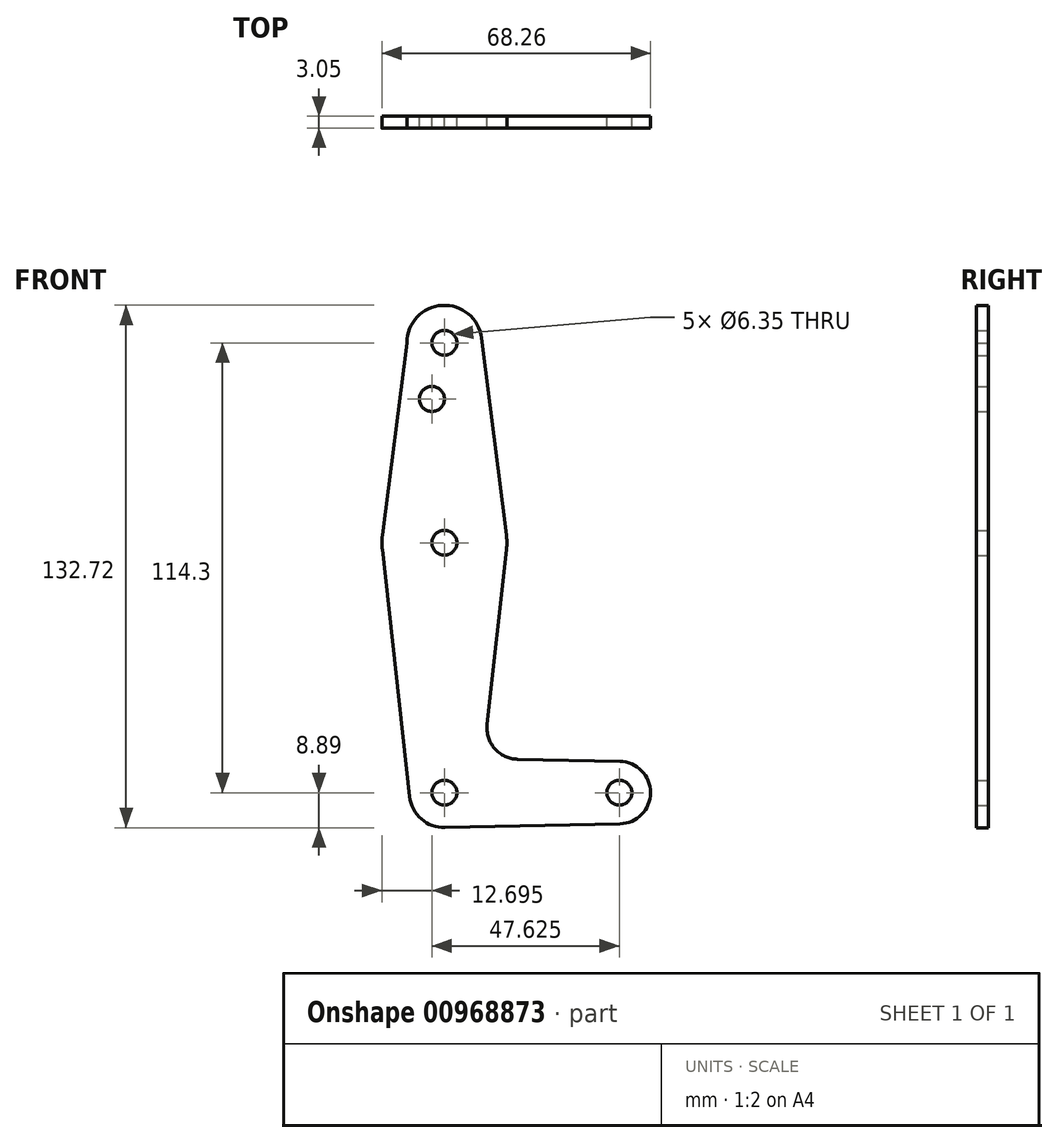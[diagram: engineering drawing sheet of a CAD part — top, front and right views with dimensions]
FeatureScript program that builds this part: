
annotation { "Feature Type Name" : "Feature", "Feature Type Description" : "" }
export const myFeature = defineFeature(function(context is Context, id is Id, definition is map)
    precondition{}
    {
        {
            var Q0;
            Q0=qCreatedBy(makeId("Front.planeOp"),FACE);
            var sketch = newSketch(context, id + "F0", { "sketchPlane" : qUnion([Q0])});
            skCircle(sketch, "E0", {"center": v(0, 114.3) * mm, "radius": 9.53 * mm});
            skCircle(sketch, "E1", {"center": v(0, 63.5) * mm, "radius": 15.88 * mm});
            skCircle(sketch, "E2", {"center": v(0, 0) * mm, "radius": 8.9 * mm});
            skCircle(sketch, "E3", {"center": v(44.45, 0) * mm, "radius": 7.94 * mm});
            skLineSegment(sketch, "E4", {"start": v(-9.52, 114.3) * mm, "end": v(-15.75, 65.5) * mm});
            skLineSegment(sketch, "E5", {"start": v(-15.78, 61.75) * mm, "end": v(-8.84, -0.98) * mm});
            skLineSegment(sketch, "E6", {"start": v(15.78, 61.75) * mm, "end": v(10.86, 17.32) * mm});
            skLineSegment(sketch, "E7", {"start": v(0.2, -8.89) * mm, "end": v(44.62, -7.94) * mm});
            skLineSegment(sketch, "E8", {"start": v(44.62, 7.94) * mm, "end": v(18.6, 8.5) * mm});
            skLineSegment(sketch, "E9", {"start": v(9.45, 115.5) * mm, "end": v(15.75, 65.48) * mm});
            skCircle(sketch, "E10", {"center": v(0, 114.3) * mm, "radius": 3.18 * mm});
            skCircle(sketch, "E11", {"center": v(0, 63.5) * mm, "radius": 3.18 * mm});
            skCircle(sketch, "E12", {"center": v(0, 0) * mm, "radius": 3.18 * mm});
            skCircle(sketch, "E13", {"center": v(44.45, 0) * mm, "radius": 3.18 * mm});
            skArc(sketch, "E14.filletArc", {"start": v(10.86, 17.32) * mm, "mid": v(12.78, 11.2) * mm, "end": v(18.6, 8.5) * mm});
            skCircle(sketch, "E15", {"center": v(-3.18, 100.03) * mm, "radius": 3.18 * mm});
            skSolve(sketch);
        }
        {
            var Q0;
            Q0 = qSketchRegion(id + "F0", true);
            extrude(context, id + "F1", {"entities" : qUnion([Q0]), "depth" : 3.05 * mm, "offsetDistance" : 25.4 * mm});
        }
    });
